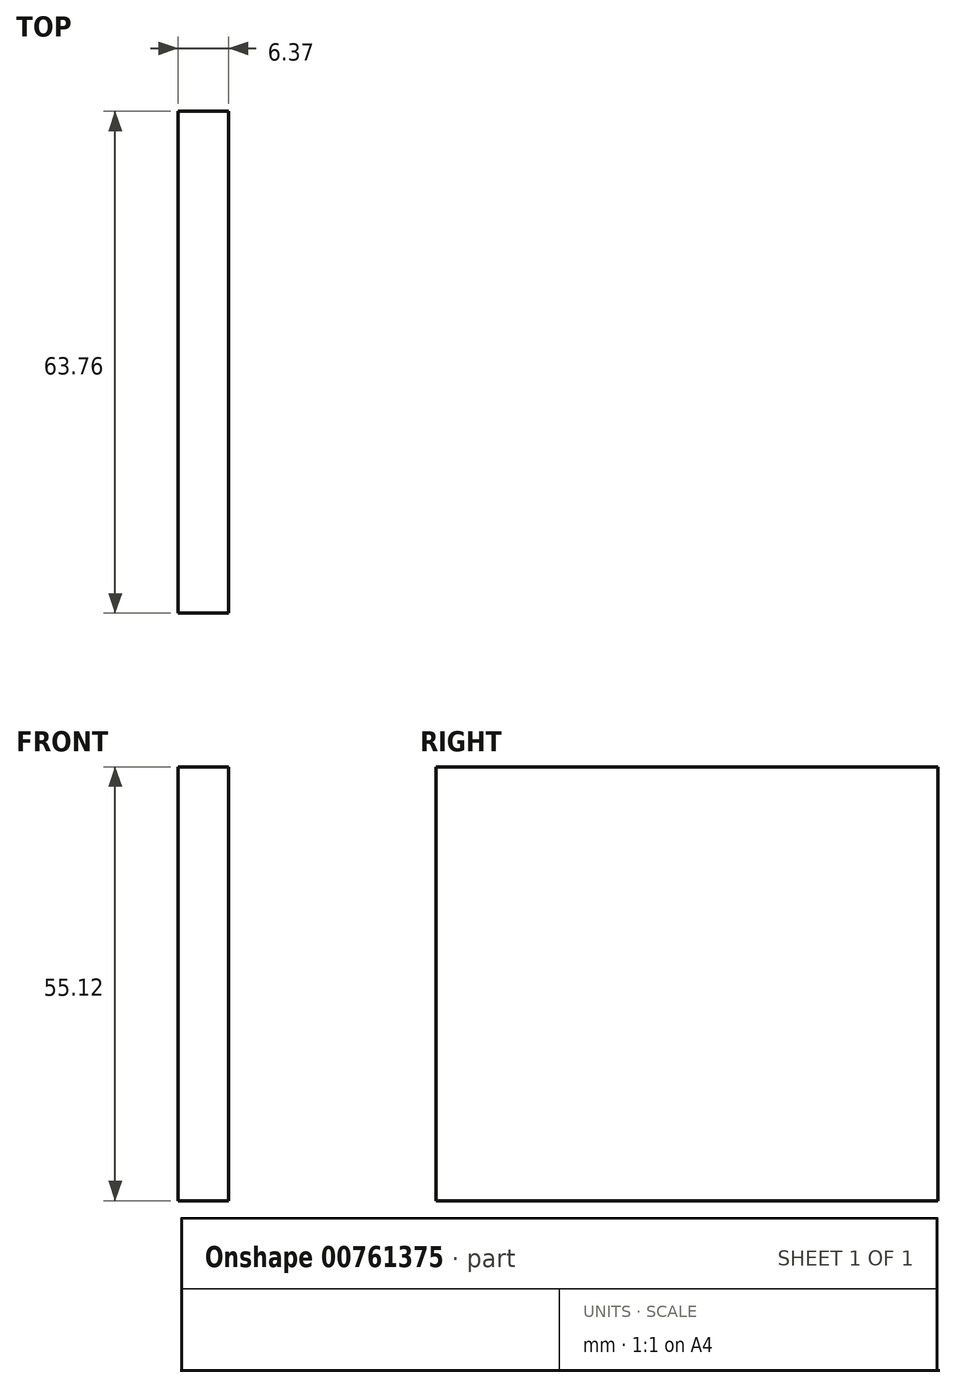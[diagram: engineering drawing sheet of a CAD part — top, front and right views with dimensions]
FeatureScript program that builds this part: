
annotation { "Feature Type Name" : "Feature", "Feature Type Description" : "" }
export const myFeature = defineFeature(function(context is Context, id is Id, definition is map)
    precondition{}
    {
        {
            var Q0;
            Q0=qCreatedBy(makeId("Top.planeOp"),FACE);
            var sketch = newSketch(context, id + "F0", { "sketchPlane" : qUnion([Q0])});
            skLineSegment(sketch, "E0.bottom", {"start": v(-39.1, 36.66) * mm, "end": v(-32.72, 36.66) * mm});
            skLineSegment(sketch, "E0.top", {"start": v(-39.1, -27.1) * mm, "end": v(-32.72, -27.1) * mm});
            skLineSegment(sketch, "E0.left", {"start": v(-39.1, 36.66) * mm, "end": v(-39.1, -27.1) * mm});
            skLineSegment(sketch, "E0.right", {"start": v(-32.72, 36.66) * mm, "end": v(-32.72, -27.1) * mm});
            skSolve(sketch);
        }
        {
            var Q0;
            Q0=makeQuery(id+"F0.imprint","IMPRINT",FACE,{"disambiguationData":[TD([[makeQuery(id+"F0.imprint","IMPRINT",EDGE,{"derivedFrom":sQuery(id+"F0.wireOp",EDGE,"E0.bottom")}),-1.0]])]});
            extrude(context, id + "F1", {"entities" : qUnion([Q0]), "depth" : 55.12 * mm, "offsetDistance" : 25.4 * mm});
        }
    });
